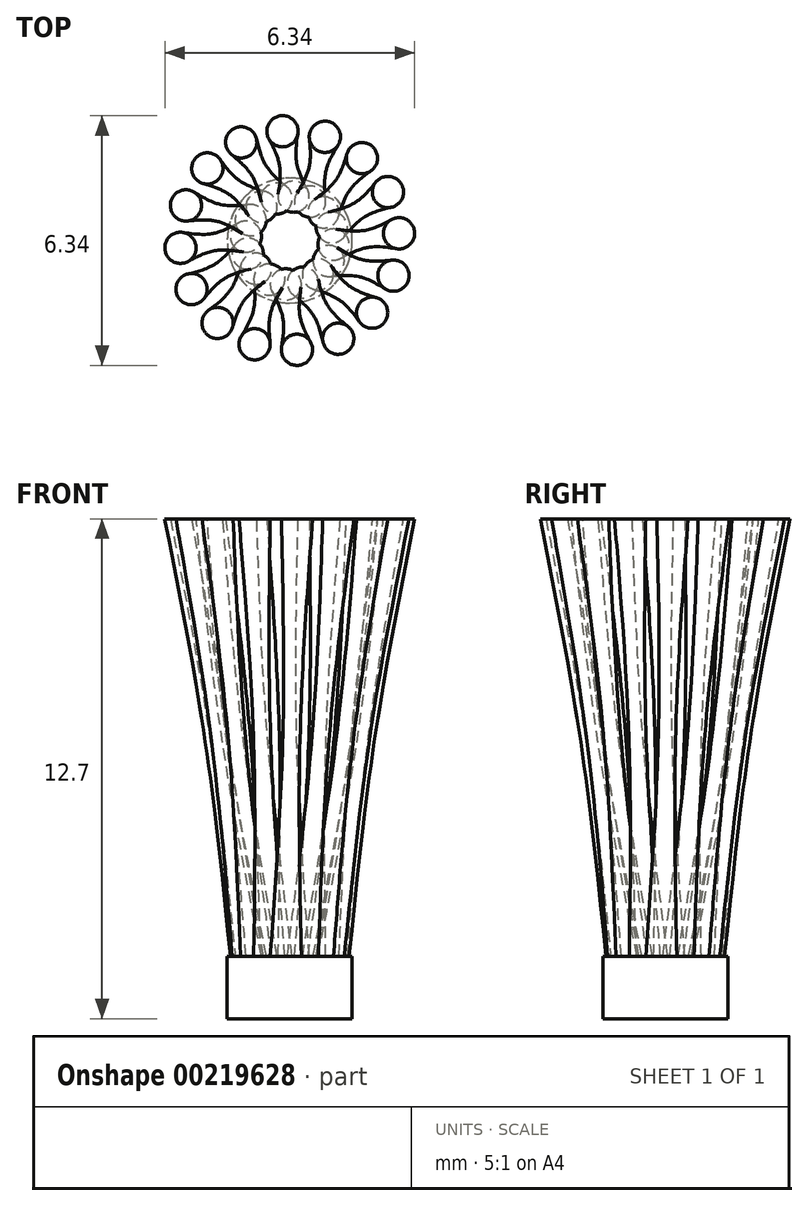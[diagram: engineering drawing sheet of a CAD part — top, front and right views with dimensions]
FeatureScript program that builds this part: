
annotation { "Feature Type Name" : "Feature", "Feature Type Description" : "" }
export const myFeature = defineFeature(function(context is Context, id is Id, definition is map)
    precondition{}
    {
        {
            var Q0;
            Q0=qCreatedBy(makeId("Top.planeOp"),FACE);
            var sketch = newSketch(context, id + "F0", { "sketchPlane" : qUnion([Q0])});
            skCircle(sketch, "E0", {"center": v(0, 0) * mm, "radius": 1.59 * mm});
            skSolve(sketch);
        }
        {
            var Q0;
            Q0=qCreatedBy(makeId("Top.planeOp"),FACE);
            cPlane(context, id + "F1", {"entities" : qUnion([Q0]), "cplaneType" : CPlaneType.OFFSET, "offset" : 12.7 * mm, "width" : 152.4 * mm, "height" : 152.4 * mm});
        }
        {
            var Q0;
            Q0=qCreatedBy(id+"F1.planeOp",FACE);
            var sketch = newSketch(context, id + "F2", { "sketchPlane" : qUnion([Q0])});
            skCircle(sketch, "E1", {"center": v(-1.83, -2.1) * mm, "radius": 0.4 * mm});
            skSolve(sketch);
        }
        {
            var Q0;
            Q0=qSketchRegion(id+"F0",true);
            extrude(context, id + "F3", {"entities" : qUnion([Q0]), "depth" : 1.59 * mm});
        }
        {
            var Q0;
            Q0=makeQuery(id+"F3.opExtrude","CAP_FACE",FACE,{"disambiguationData":[OSD([sQuery(id+"F0.wireOp",EDGE,"E0")])],"isStart":false});
            var sketch = newSketch(context, id + "F4", { "sketchPlane" : qUnion([Q0])});
            skCircle(sketch, "E2", {"center": v(-0.86, -0.72) * mm, "radius": 0.4 * mm});
            skSolve(sketch);
        }
        {
            var Q1;
            Q1=makeQuery(id+"F2.imprint","IMPRINT",FACE,{"disambiguationData":[TD([[makeQuery(id+"F2.imprint","IMPRINT",EDGE,{"derivedFrom":sQuery(id+"F2.wireOp",EDGE,"E1")}),1.0]])]});
            var Q2;
            Q2=makeQuery(id+"F4.imprint","IMPRINT",FACE,{"disambiguationData":[TD([[makeQuery(id+"F4.imprint","IMPRINT",EDGE,{"derivedFrom":sQuery(id+"F4.wireOp",EDGE,"E2")}),1.0]])]});
            loft(context, id + "F5", {"sheetProfilesArray" : [{ "sheetProfileEntities" : qUnion([Q1]) }, { "sheetProfileEntities" : qUnion([Q2]) }]});
        }
        {
            var Q0;
            Q0=makeQuery(id+"F5.opLoft","SWEPT_BODY",BODY,{"disambiguationData":[OSD([makeQuery(id+"F2.imprint","IMPRINT",FACE,{"disambiguationData":[TD([[makeQuery(id+"F2.imprint","IMPRINT",EDGE,{"derivedFrom":sQuery(id+"F2.wireOp",EDGE,"E1")}),1.0]])]}),makeQuery(id+"F4.imprint","IMPRINT",FACE,{"disambiguationData":[TD([[makeQuery(id+"F4.imprint","IMPRINT",EDGE,{"derivedFrom":sQuery(id+"F4.wireOp",EDGE,"E2")}),1.0]])]})])]});
            var Q1;
            Q1=sQuery(id+"F0.wireOp",EDGE,"E0");
            circularPattern(context, id + "F6", {"entities" : qUnion([Q0]), "axis" : qUnion([Q1]), "angle" : 360 * degree, "instanceCount" : 16, "equalSpace" : true});
        }
    });
